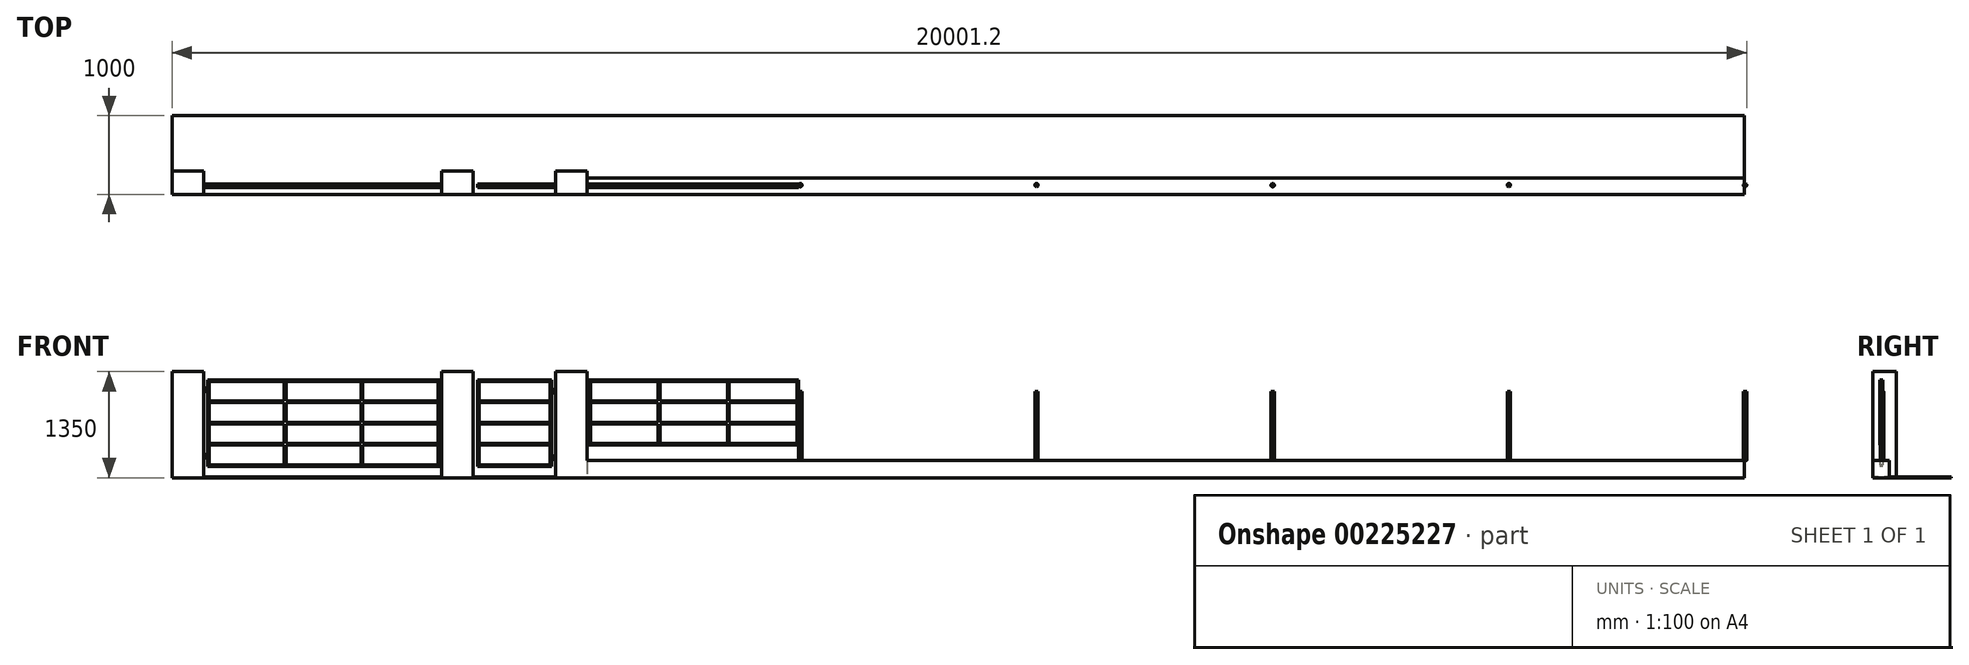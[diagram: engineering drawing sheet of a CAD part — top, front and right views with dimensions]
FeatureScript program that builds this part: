
annotation { "Feature Type Name" : "Feature", "Feature Type Description" : "" }
export const myFeature = defineFeature(function(context is Context, id is Id, definition is map)
    precondition{}
    {
        {
            var Q0;
            Q0=qCreatedBy(makeId("Front.planeOp"),FACE);
            var sketch = newSketch(context, id + "F0", { "sketchPlane" : qUnion([Q0])});
            skLineSegment(sketch, "E0.bottom", {"start": v(0, 0) * mm, "end": v(19970, 0) * mm});
            skLineSegment(sketch, "E0.top", {"start": v(0, -10) * mm, "end": v(19970, -10) * mm});
            skLineSegment(sketch, "E0.left", {"start": v(0, 0) * mm, "end": v(0, -10) * mm});
            skLineSegment(sketch, "E0.right", {"start": v(19970, 0) * mm, "end": v(19970, -10) * mm});
            skSolve(sketch);
        }
        {
            var Q0;
            Q0 = qSketchRegion(id + "F0", true);
            extrude(context, id + "F1", {"entities" : qUnion([Q0]), "oppositeDirection" : true, "depth" : 1000 * mm});
        }
        {
            var Q0;
            Q0=makeQuery(id+"F1.opExtrude","SWEPT_FACE",FACE,{"disambiguationData":[OSD([sQuery(id+"F0.wireOp",EDGE,"E0.bottom")])]});
            var sketch = newSketch(context, id + "F2", { "sketchPlane" : qUnion([Q0])});
            skLineSegment(sketch, "E1.bottom", {"start": v(0, 300) * mm, "end": v(400, 300) * mm});
            skLineSegment(sketch, "E1.top", {"start": v(0, 0) * mm, "end": v(400, 0) * mm});
            skLineSegment(sketch, "E1.left", {"start": v(0, 300) * mm, "end": v(0, 0) * mm});
            skLineSegment(sketch, "E1.right", {"start": v(400, 300) * mm, "end": v(400, 0) * mm});
            skLineSegment(sketch, "E2.bottom", {"start": v(3420, 0) * mm, "end": v(3820, 0) * mm});
            skLineSegment(sketch, "E2.top", {"start": v(3420, 300) * mm, "end": v(3820, 300) * mm});
            skLineSegment(sketch, "E2.left", {"start": v(3420, 0) * mm, "end": v(3420, 300) * mm});
            skLineSegment(sketch, "E2.right", {"start": v(3820, 0) * mm, "end": v(3820, 300) * mm});
            skLineSegment(sketch, "E3.bottom", {"start": v(4870, 0) * mm, "end": v(5270, 0) * mm});
            skLineSegment(sketch, "E3.top", {"start": v(4870, 300) * mm, "end": v(5270, 300) * mm});
            skLineSegment(sketch, "E3.left", {"start": v(4870, 0) * mm, "end": v(4870, 300) * mm});
            skLineSegment(sketch, "E3.right", {"start": v(5270, 0) * mm, "end": v(5270, 300) * mm});
            skSolve(sketch);
        }
        {
            var Q0;
            Q0 = qSketchRegion(id + "F2", true);
            extrude(context, id + "F3", {"entities" : qUnion([Q0]), "operationType" : NewBodyOperationType.ADD, "depth" : 1340 * mm});
        }
        {
            var Q0;
            Q0=makeQuery(id+"F3.opExtrude","CAP_FACE",FACE,{"disambiguationData":[OSD([sQuery(id+"F2.wireOp",EDGE,"E1.bottom"),sQuery(id+"F2.wireOp",EDGE,"E1.top"),sQuery(id+"F2.wireOp",EDGE,"E1.left"),sQuery(id+"F2.wireOp",EDGE,"E1.right")])],"isStart":false});
            var sketch = newSketch(context, id + "F4", { "sketchPlane" : qUnion([Q0])});
            skLineSegment(sketch, "E4.bottom", {"start": v(-50, 350) * mm, "end": v(450, 350) * mm});
            skLineSegment(sketch, "E4.top", {"start": v(-50, -50) * mm, "end": v(450, -50) * mm});
            skLineSegment(sketch, "E4.left", {"start": v(-50, 350) * mm, "end": v(-50, -50) * mm});
            skLineSegment(sketch, "E4.right", {"start": v(450, 350) * mm, "end": v(450, -50) * mm});
            skLineSegment(sketch, "E5", {"start": v(0, 150) * mm, "end": v(523.62, 150) * mm, "construction": true});
            skPoint(sketch, "E5.endSnap0", {"position": v(0, 150) * mm});
            skLineSegment(sketch, "E6", {"start": v(200, 300) * mm, "end": v(200, 45.97) * mm, "construction": true});
            skPoint(sketch, "E6.endSnap0", {"position": v(200, 0) * mm});
            skLineSegment(sketch, "E7", {"start": v(3620, 403.37) * mm, "end": v(3620, 52.03) * mm, "construction": true});
            skLineSegment(sketch, "E8", {"start": v(3394.91, 150) * mm, "end": v(3852.26, 150) * mm, "construction": true});
            skLineSegment(sketch, "E9.bottom", {"start": v(3370, 350) * mm, "end": v(3870, 350) * mm});
            skLineSegment(sketch, "E9.top", {"start": v(3370, -50) * mm, "end": v(3870, -50) * mm});
            skLineSegment(sketch, "E9.left", {"start": v(3370, 350) * mm, "end": v(3370, -50) * mm});
            skLineSegment(sketch, "E9.right", {"start": v(3870, 350) * mm, "end": v(3870, -50) * mm});
            skLineSegment(sketch, "E10", {"start": v(4712.44, 150) * mm, "end": v(5318.2, 150) * mm, "construction": true});
            skLineSegment(sketch, "E11", {"start": v(5070, 485.15) * mm, "end": v(5070, -156.96) * mm, "construction": true});
            skLineSegment(sketch, "E12.bottom", {"start": v(4820, 350) * mm, "end": v(5320, 350) * mm});
            skLineSegment(sketch, "E12.top", {"start": v(4820, -50) * mm, "end": v(5320, -50) * mm});
            skLineSegment(sketch, "E12.left", {"start": v(4820, 350) * mm, "end": v(4820, -50) * mm});
            skLineSegment(sketch, "E12.right", {"start": v(5320, 350) * mm, "end": v(5320, -50) * mm});
            skSolve(sketch);
        }
        {
            var Q0;
            Q0=makeQuery(id+"F1.opExtrude","SWEPT_FACE",FACE,{"disambiguationData":[OSD([sQuery(id+"F0.wireOp",EDGE,"E0.bottom")])]});
            var sketch = newSketch(context, id + "F5", { "sketchPlane" : qUnion([Q0])});
            skLineSegment(sketch, "E13", {"start": v(5270, 0) * mm, "end": v(19970, 0) * mm});
            skLineSegment(sketch, "E14", {"start": v(5270, 210) * mm, "end": v(19970, 210) * mm});
            skLineSegment(sketch, "E15", {"start": v(19970, 210) * mm, "end": v(19970, 0) * mm});
            skLineSegment(sketch, "E16", {"start": v(5270, 210) * mm, "end": v(5270, 0) * mm});
            skSolve(sketch);
        }
        {
            var Q0;
            Q0 = qSketchRegion(id + "F5", true);
            extrude(context, id + "F6", {"entities" : qUnion([Q0]), "operationType" : NewBodyOperationType.ADD, "depth" : 210 * mm});
        }
        {
            var Q0;
            Q0=makeQuery(id+"F6.opExtrude","CAP_FACE",FACE,{"disambiguationData":[OSD([sQuery(id+"F5.wireOp",EDGE,"E13"),sQuery(id+"F5.wireOp",EDGE,"E14"),sQuery(id+"F5.wireOp",EDGE,"E15"),sQuery(id+"F5.wireOp",EDGE,"E16")])],"isStart":false});
            var sketch = newSketch(context, id + "F7", { "sketchPlane" : qUnion([Q0])});
            skLineSegment(sketch, "E17", {"start": v(6497.43, 118) * mm, "end": v(10628.2, 118) * mm, "construction": true});
            skCircle(sketch, "E18", {"center": v(7980, 118) * mm, "radius": 21.25 * mm});
            skCircle(sketch, "E19.1.0.0", {"center": v(10980, 118) * mm, "radius": 21.25 * mm});
            skCircle(sketch, "E19.2.0.0", {"center": v(13980, 118) * mm, "radius": 21.25 * mm});
            skLineSegment(sketch, "E19.direction1", {"start": v(7980, 118) * mm, "end": v(10980, 118) * mm, "construction": true});
            skCircle(sketch, "E20.0.3.0", {"center": v(16980, 118) * mm, "radius": 21.25 * mm});
            skCircle(sketch, "E21.0.4.0", {"center": v(19980, 118) * mm, "radius": 21.25 * mm});
            skSolve(sketch);
        }
        {
            var Q0;
            Q0 = qSketchRegion(id + "F7", true);
            extrude(context, id + "F8", {"entities" : qUnion([Q0]), "operationType" : NewBodyOperationType.ADD, "depth" : 880 * mm});
        }
        {
            var Q0;
            Q0=qCreatedBy(makeId("Front.planeOp"),FACE);
            cPlane(context, id + "F9", {"entities" : qUnion([Q0]), "cplaneType" : CPlaneType.OFFSET, "offset" : 90 * mm, "oppositeDirection" : true, "width" : 150 * mm, "height" : 150 * mm});
        }
        {
            var Q0;
            Q0=qCreatedBy(id+"F9.planeOp",FACE);
            var sketch = newSketch(context, id + "F10", { "sketchPlane" : qUnion([Q0])});
            skLineSegment(sketch, "E22.bottom", {"start": v(450, 1235) * mm, "end": v(3395, 1235) * mm});
            skLineSegment(sketch, "E22.top", {"start": v(450, 135) * mm, "end": v(3395, 135) * mm});
            skLineSegment(sketch, "E22.left", {"start": v(450, 1235) * mm, "end": v(450, 135) * mm});
            skLineSegment(sketch, "E22.right", {"start": v(3395, 1235) * mm, "end": v(3395, 135) * mm});
            skLineSegment(sketch, "E23.bottom", {"start": v(470, 1215) * mm, "end": v(1425, 1215) * mm});
            skLineSegment(sketch, "E23.top", {"start": v(470, 155) * mm, "end": v(1425, 155) * mm});
            skLineSegment(sketch, "E23.left", {"start": v(470, 1215) * mm, "end": v(470, 965) * mm});
            skLineSegment(sketch, "E23.right", {"start": v(3375, 1215) * mm, "end": v(3375, 965) * mm});
            skLineSegment(sketch, "E24.bottom", {"start": v(470, 965) * mm, "end": v(1425, 965) * mm});
            skLineSegment(sketch, "E24.top", {"start": v(470, 945) * mm, "end": v(1425, 945) * mm});
            skLineSegment(sketch, "E25.bottom", {"start": v(470, 695) * mm, "end": v(1425, 695) * mm});
            skLineSegment(sketch, "E25.top", {"start": v(470, 675) * mm, "end": v(1425, 675) * mm});
            skLineSegment(sketch, "E26.left", {"start": v(1425, 1215) * mm, "end": v(1425, 965) * mm});
            skLineSegment(sketch, "E26.right", {"start": v(1445, 1215) * mm, "end": v(1445, 965) * mm});
            skLineSegment(sketch, "E27.left", {"start": v(2400, 1215) * mm, "end": v(2400, 965) * mm});
            skLineSegment(sketch, "E27.right", {"start": v(2420, 1215) * mm, "end": v(2420, 965) * mm});
            skLineSegment(sketch, "E28.bottom", {"start": v(470, 425) * mm, "end": v(1425, 425) * mm});
            skLineSegment(sketch, "E28.top", {"start": v(470, 405) * mm, "end": v(1425, 405) * mm});
            skLineSegment(sketch, "E29", {"start": v(3252.9, 1235) * mm, "end": v(5403.26, 1235) * mm, "construction": true});
            skLineSegment(sketch, "E30", {"start": v(3256.67, 135) * mm, "end": v(5523.98, 135) * mm, "construction": true});
            skLineSegment(sketch, "E31.bottom", {"start": v(3880, 1235) * mm, "end": v(4820, 1235) * mm});
            skLineSegment(sketch, "E31.top", {"start": v(3880, 135) * mm, "end": v(4820, 135) * mm});
            skLineSegment(sketch, "E31.left", {"start": v(3880, 1235) * mm, "end": v(3880, 135) * mm});
            skLineSegment(sketch, "E31.right", {"start": v(4820, 1235) * mm, "end": v(4820, 135) * mm});
            skLineSegment(sketch, "E32.bottom", {"start": v(3900, 1215) * mm, "end": v(4800, 1215) * mm});
            skLineSegment(sketch, "E32.top", {"start": v(3900, 155) * mm, "end": v(4800, 155) * mm});
            skLineSegment(sketch, "E32.left", {"start": v(3900, 1215) * mm, "end": v(3900, 965) * mm});
            skLineSegment(sketch, "E32.right", {"start": v(4800, 1215) * mm, "end": v(4800, 965) * mm});
            skLineSegment(sketch, "E33.bottom", {"start": v(3900, 945) * mm, "end": v(4800, 945) * mm});
            skLineSegment(sketch, "E33.top", {"start": v(3900, 965) * mm, "end": v(4800, 965) * mm});
            skLineSegment(sketch, "E34.trimOffspring", {"start": v(470, 945) * mm, "end": v(470, 695) * mm});
            skLineSegment(sketch, "E35.trimOffspring", {"start": v(1445, 1215) * mm, "end": v(2400, 1215) * mm});
            skLineSegment(sketch, "E36.trimOffspring", {"start": v(1445, 965) * mm, "end": v(2400, 965) * mm});
            skLineSegment(sketch, "E37.trimOffspring", {"start": v(1425, 945) * mm, "end": v(1425, 695) * mm});
            skLineSegment(sketch, "E38.trimOffspring", {"start": v(1445, 945) * mm, "end": v(1445, 695) * mm});
            skLineSegment(sketch, "E39.trimOffspring", {"start": v(1445, 945) * mm, "end": v(2400, 945) * mm});
            skLineSegment(sketch, "E40.trimOffspring", {"start": v(470, 675) * mm, "end": v(470, 425) * mm});
            skLineSegment(sketch, "E41.trimOffspring", {"start": v(1425, 675) * mm, "end": v(1425, 425) * mm});
            skLineSegment(sketch, "E42.trimOffspring", {"start": v(1445, 695) * mm, "end": v(2400, 695) * mm});
            skLineSegment(sketch, "E43.trimOffspring", {"start": v(1445, 675) * mm, "end": v(1445, 425) * mm});
            skLineSegment(sketch, "E44.trimOffspring", {"start": v(1445, 675) * mm, "end": v(2400, 675) * mm});
            skLineSegment(sketch, "E45.trimOffspring", {"start": v(1445, 425) * mm, "end": v(2400, 425) * mm});
            skLineSegment(sketch, "E46.trimOffspring", {"start": v(1445, 405) * mm, "end": v(1445, 155) * mm});
            skLineSegment(sketch, "E47.trimOffspring", {"start": v(1445, 405) * mm, "end": v(2400, 405) * mm});
            skLineSegment(sketch, "E48.trimOffspring", {"start": v(1425, 405) * mm, "end": v(1425, 155) * mm});
            skLineSegment(sketch, "E49.trimOffspring", {"start": v(470, 405) * mm, "end": v(470, 155) * mm});
            skLineSegment(sketch, "E50.trimOffspring", {"start": v(1445, 155) * mm, "end": v(2400, 155) * mm});
            skLineSegment(sketch, "E51.trimOffspring", {"start": v(2420, 155) * mm, "end": v(3375, 155) * mm});
            skLineSegment(sketch, "E52.trimOffspring", {"start": v(2400, 405) * mm, "end": v(2400, 155) * mm});
            skLineSegment(sketch, "E53.trimOffspring", {"start": v(2420, 425) * mm, "end": v(3375, 425) * mm});
            skLineSegment(sketch, "E54.trimOffspring", {"start": v(2420, 405) * mm, "end": v(2420, 155) * mm});
            skLineSegment(sketch, "E55.trimOffspring", {"start": v(2420, 405) * mm, "end": v(3375, 405) * mm});
            skLineSegment(sketch, "E56.trimOffspring", {"start": v(2400, 675) * mm, "end": v(2400, 425) * mm});
            skLineSegment(sketch, "E57.trimOffspring", {"start": v(2420, 695) * mm, "end": v(3375, 695) * mm});
            skLineSegment(sketch, "E58.trimOffspring", {"start": v(2420, 675) * mm, "end": v(2420, 425) * mm});
            skLineSegment(sketch, "E59.trimOffspring", {"start": v(2420, 675) * mm, "end": v(3375, 675) * mm});
            skLineSegment(sketch, "E60.trimOffspring", {"start": v(2400, 945) * mm, "end": v(2400, 695) * mm});
            skLineSegment(sketch, "E61.trimOffspring", {"start": v(2420, 945) * mm, "end": v(2420, 695) * mm});
            skLineSegment(sketch, "E62.trimOffspring", {"start": v(2420, 945) * mm, "end": v(3375, 945) * mm});
            skLineSegment(sketch, "E63.trimOffspring", {"start": v(2420, 965) * mm, "end": v(3375, 965) * mm});
            skLineSegment(sketch, "E64.trimOffspring", {"start": v(2420, 1215) * mm, "end": v(3375, 1215) * mm});
            skLineSegment(sketch, "E65.trimOffspring", {"start": v(3375, 945) * mm, "end": v(3375, 695) * mm});
            skLineSegment(sketch, "E66.trimOffspring", {"start": v(3375, 675) * mm, "end": v(3375, 425) * mm});
            skLineSegment(sketch, "E67.trimOffspring", {"start": v(3375, 405) * mm, "end": v(3375, 155) * mm});
            skLineSegment(sketch, "E68.trimOffspring", {"start": v(4800, 405) * mm, "end": v(4800, 155) * mm});
            skLineSegment(sketch, "E69.trimOffspring", {"start": v(4800, 945) * mm, "end": v(4800, 695) * mm});
            skLineSegment(sketch, "E70", {"start": v(3375, 695) * mm, "end": v(4240.31, 695) * mm, "construction": true});
            skLineSegment(sketch, "E71", {"start": v(3375, 965) * mm, "end": v(4341.72, 965) * mm, "construction": true});
            skLineSegment(sketch, "E72", {"start": v(3375, 425) * mm, "end": v(4240.39, 425) * mm, "construction": true});
            skLineSegment(sketch, "E73", {"start": v(3900, 695) * mm, "end": v(4800, 695) * mm});
            skLineSegment(sketch, "E74", {"start": v(3900, 675) * mm, "end": v(4800, 675) * mm});
            skLineSegment(sketch, "E75", {"start": v(3900, 945) * mm, "end": v(3900, 695) * mm});
            skLineSegment(sketch, "E76", {"start": v(3900, 425) * mm, "end": v(4800, 425) * mm});
            skLineSegment(sketch, "E77", {"start": v(3900, 405) * mm, "end": v(4800, 405) * mm});
            skLineSegment(sketch, "E78", {"start": v(3900, 675) * mm, "end": v(3900, 425) * mm});
            skLineSegment(sketch, "E79", {"start": v(4800, 675) * mm, "end": v(4800, 425) * mm});
            skLineSegment(sketch, "E80.trimOffspring", {"start": v(3900, 405) * mm, "end": v(3900, 155) * mm});
            skSolve(sketch);
        }
        {
            var Q0;
            Q0 = qSketchRegion(id + "F10", true);
            extrude(context, id + "F11", {"entities" : qUnion([Q0]), "oppositeDirection" : true, "depth" : 40 * mm});
        }
        {
            var Q0;
            Q0=qCreatedBy(id+"F9.planeOp",FACE);
            var sketch = newSketch(context, id + "F12", { "sketchPlane" : qUnion([Q0])});
            skLineSegment(sketch, "E81.bottom", {"start": v(400, 1130) * mm, "end": v(445, 1130) * mm});
            skLineSegment(sketch, "E81.top", {"start": v(400, 1090) * mm, "end": v(445, 1090) * mm});
            skLineSegment(sketch, "E81.left", {"start": v(400, 1130) * mm, "end": v(400, 1090) * mm});
            skLineSegment(sketch, "E81.right", {"start": v(445, 1130) * mm, "end": v(445, 1090) * mm});
            skLineSegment(sketch, "E82.bottom", {"start": v(400, 285) * mm, "end": v(445, 285) * mm});
            skLineSegment(sketch, "E82.top", {"start": v(400, 245) * mm, "end": v(445, 245) * mm});
            skLineSegment(sketch, "E82.left", {"start": v(400, 285) * mm, "end": v(400, 245) * mm});
            skLineSegment(sketch, "E82.right", {"start": v(445, 285) * mm, "end": v(445, 245) * mm});
            skLineSegment(sketch, "E83.bottom", {"start": v(4825, 1110) * mm, "end": v(4870, 1110) * mm});
            skLineSegment(sketch, "E83.top", {"start": v(4825, 1070) * mm, "end": v(4870, 1070) * mm});
            skLineSegment(sketch, "E83.left", {"start": v(4825, 1110) * mm, "end": v(4825, 1070) * mm});
            skLineSegment(sketch, "E83.right", {"start": v(4870, 1110) * mm, "end": v(4870, 1070) * mm});
            skLineSegment(sketch, "E84.bottom", {"start": v(4825, 265) * mm, "end": v(4870, 265) * mm});
            skLineSegment(sketch, "E84.top", {"start": v(4825, 225) * mm, "end": v(4870, 225) * mm});
            skLineSegment(sketch, "E84.left", {"start": v(4825, 265) * mm, "end": v(4825, 225) * mm});
            skLineSegment(sketch, "E84.right", {"start": v(4870, 265) * mm, "end": v(4870, 225) * mm});
            skSolve(sketch);
        }
        {
            var Q0;
            Q0 = qSketchRegion(id + "F12", true);
            extrude(context, id + "F13", {"entities" : qUnion([Q0]), "operationType" : NewBodyOperationType.ADD, "oppositeDirection" : true, "depth" : 45 * mm});
        }
        {
            var Q0;
            Q0=qCreatedBy(id+"F9.planeOp",FACE);
            var sketch = newSketch(context, id + "F14", { "sketchPlane" : qUnion([Q0])});
            skLineSegment(sketch, "E85", {"start": v(4723.12, 1235) * mm, "end": v(6598.08, 1235) * mm, "construction": true});
            skLineSegment(sketch, "E86", {"start": v(4741.98, 965) * mm, "end": v(6175, 965) * mm, "construction": true});
            skLineSegment(sketch, "E87", {"start": v(4723.12, 695) * mm, "end": v(6175, 695) * mm, "construction": true});
            skLineSegment(sketch, "E88", {"start": v(4758.96, 405) * mm, "end": v(5703.99, 405) * mm, "construction": true});
            skLineSegment(sketch, "E89.bottom", {"start": v(5295, 1235) * mm, "end": v(7955, 1235) * mm});
            skLineSegment(sketch, "E89.top", {"start": v(5295, 405) * mm, "end": v(5703.99, 405) * mm});
            skLineSegment(sketch, "E89.left", {"start": v(5295, 1235) * mm, "end": v(5295, 405) * mm});
            skLineSegment(sketch, "E89.right", {"start": v(7955, 1235) * mm, "end": v(7955, 405) * mm});
            skLineSegment(sketch, "E90.bottom", {"start": v(5315, 1215) * mm, "end": v(6175, 1215) * mm});
            skLineSegment(sketch, "E90.top", {"start": v(5315, 425) * mm, "end": v(6175, 425) * mm});
            skLineSegment(sketch, "E90.left", {"start": v(5315, 1215) * mm, "end": v(5315, 965) * mm});
            skLineSegment(sketch, "E90.right", {"start": v(7935, 1215) * mm, "end": v(7935, 965) * mm});
            skLineSegment(sketch, "E91.bottom", {"start": v(5315, 965) * mm, "end": v(6175, 965) * mm});
            skLineSegment(sketch, "E91.top", {"start": v(5315, 945) * mm, "end": v(6175, 945) * mm});
            skLineSegment(sketch, "E92.bottom", {"start": v(5315, 695) * mm, "end": v(6175, 695) * mm});
            skLineSegment(sketch, "E92.top", {"start": v(5315, 675) * mm, "end": v(6175, 675) * mm});
            skLineSegment(sketch, "E93.left", {"start": v(6175, 1215) * mm, "end": v(6175, 965) * mm});
            skLineSegment(sketch, "E93.right", {"start": v(6195, 1215) * mm, "end": v(6195, 965) * mm});
            skLineSegment(sketch, "E94.left", {"start": v(7055, 1215) * mm, "end": v(7055, 965) * mm});
            skLineSegment(sketch, "E94.right", {"start": v(7075, 1215) * mm, "end": v(7075, 965) * mm});
            skLineSegment(sketch, "E95.bottom", {"start": v(7395, 1215) * mm, "end": v(7415, 1215) * mm});
            skLineSegment(sketch, "E96", {"start": v(7958.75, 210) * mm, "end": v(7958.75, 1090) * mm});
            skLineSegment(sketch, "E97", {"start": v(8001.25, 1090) * mm, "end": v(8001.25, 210) * mm});
            skLineSegment(sketch, "E98", {"start": v(7980, 1013.1) * mm, "end": v(7980, 1365.23) * mm, "construction": true});
            skLineSegment(sketch, "E99.trimOffspring", {"start": v(6195, 1215) * mm, "end": v(7055, 1215) * mm});
            skLineSegment(sketch, "E100.trimOffspring", {"start": v(6195, 965) * mm, "end": v(6649.01, 965) * mm, "construction": true});
            skLineSegment(sketch, "E101.trimOffspring", {"start": v(6195, 965) * mm, "end": v(7055, 965) * mm});
            skLineSegment(sketch, "E102.trimOffspring", {"start": v(6175, 945) * mm, "end": v(6175, 695) * mm});
            skLineSegment(sketch, "E103.trimOffspring", {"start": v(6195, 945) * mm, "end": v(6195, 695) * mm});
            skLineSegment(sketch, "E104.trimOffspring", {"start": v(6195, 945) * mm, "end": v(7055, 945) * mm});
            skLineSegment(sketch, "E105.trimOffspring", {"start": v(6195, 695) * mm, "end": v(6624.5, 695) * mm, "construction": true});
            skLineSegment(sketch, "E106.trimOffspring", {"start": v(6195, 675) * mm, "end": v(7055, 675) * mm});
            skLineSegment(sketch, "E107.trimOffspring", {"start": v(6175, 675) * mm, "end": v(6175, 425) * mm});
            skLineSegment(sketch, "E108.trimOffspring", {"start": v(6195, 695) * mm, "end": v(7055, 695) * mm});
            skLineSegment(sketch, "E109.trimOffspring", {"start": v(6195, 675) * mm, "end": v(6195, 425) * mm});
            skLineSegment(sketch, "E110.trimOffspring", {"start": v(6195, 425) * mm, "end": v(7055, 425) * mm});
            skLineSegment(sketch, "E111.trimOffspring", {"start": v(5315, 675) * mm, "end": v(5315, 425) * mm});
            skLineSegment(sketch, "E112.trimOffspring", {"start": v(5315, 945) * mm, "end": v(5315, 695) * mm});
            skLineSegment(sketch, "E113.trimOffspring", {"start": v(7075, 695) * mm, "end": v(7935, 695) * mm});
            skLineSegment(sketch, "E114.trimOffspring", {"start": v(7055, 675) * mm, "end": v(7055, 425) * mm});
            skLineSegment(sketch, "E115.trimOffspring", {"start": v(7075, 675) * mm, "end": v(7075, 425) * mm});
            skLineSegment(sketch, "E116.trimOffspring", {"start": v(7075, 675) * mm, "end": v(7935, 675) * mm});
            skLineSegment(sketch, "E117.trimOffspring", {"start": v(7075, 425) * mm, "end": v(7935, 425) * mm});
            skLineSegment(sketch, "E118.trimOffspring", {"start": v(7075, 945) * mm, "end": v(7935, 945) * mm});
            skLineSegment(sketch, "E119.trimOffspring", {"start": v(7075, 965) * mm, "end": v(7935, 965) * mm});
            skLineSegment(sketch, "E120.trimOffspring", {"start": v(7055, 945) * mm, "end": v(7055, 695) * mm});
            skLineSegment(sketch, "E121.trimOffspring", {"start": v(7075, 945) * mm, "end": v(7075, 695) * mm});
            skLineSegment(sketch, "E122.trimOffspring", {"start": v(7075, 1215) * mm, "end": v(7935, 1215) * mm});
            skLineSegment(sketch, "E123.trimOffspring", {"start": v(7935, 675) * mm, "end": v(7935, 425) * mm});
            skLineSegment(sketch, "E124.trimOffspring", {"start": v(7935, 945) * mm, "end": v(7935, 695) * mm});
            skLineSegment(sketch, "E125.trimOffspring", {"start": v(5295, 405) * mm, "end": v(7955, 405) * mm});
            skSolve(sketch);
        }
        {
            var Q0;
            Q0 = qSketchRegion(id + "F14", true);
            extrude(context, id + "F15", {"entities" : qUnion([Q0]), "oppositeDirection" : true, "depth" : 40 * mm});
        }
    });
